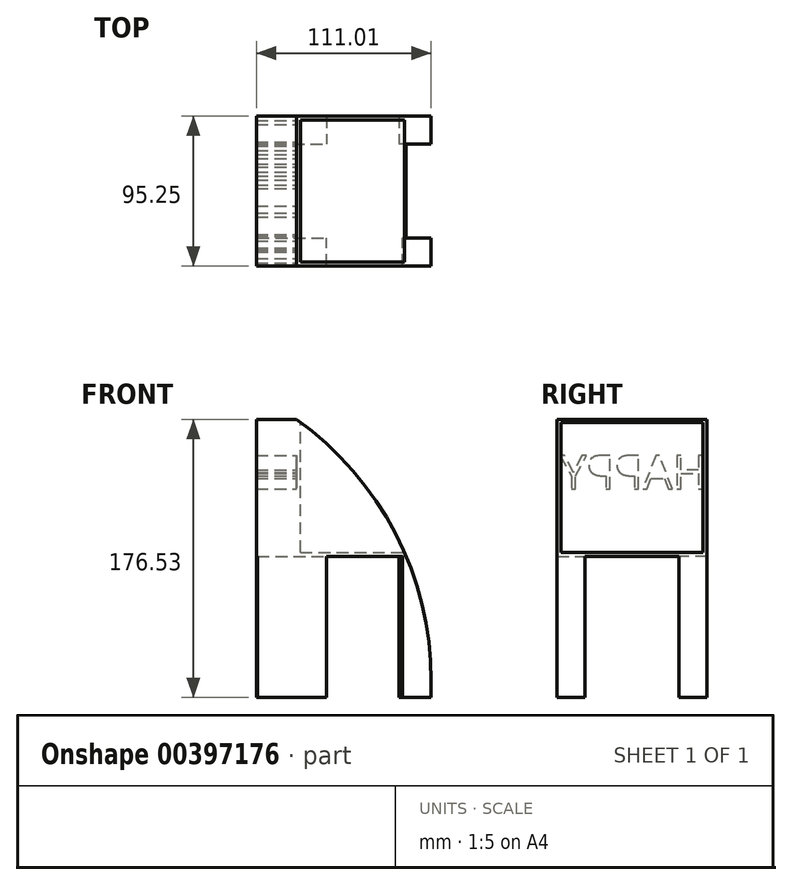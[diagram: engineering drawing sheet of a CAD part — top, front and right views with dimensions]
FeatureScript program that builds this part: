
annotation { "Feature Type Name" : "Feature", "Feature Type Description" : "" }
export const myFeature = defineFeature(function(context is Context, id is Id, definition is map)
    precondition{}
    {
        {
            var Q0;
            Q0=qCreatedBy(makeId("Front.planeOp"),FACE);
            var sketch = newSketch(context, id + "F0", { "sketchPlane" : qUnion([Q0])});
            skLineSegment(sketch, "E0.bottom", {"start": v(0, 0) * mm, "end": v(51.32, 0) * mm});
            skLineSegment(sketch, "E0.top", {"start": v(0, 35.31) * mm, "end": v(51.32, 35.31) * mm});
            skLineSegment(sketch, "E0.left", {"start": v(0, 0) * mm, "end": v(0, 35.31) * mm});
            skLineSegment(sketch, "E0.right", {"start": v(51.32, 0) * mm, "end": v(51.32, 35.31) * mm});
            skSolve(sketch);
        }
        {
            var Q0;
            Q0 = qSketchRegion(id + "F0", true);
            extrude(context, id + "F1", {"entities" : qUnion([Q0]), "depth" : 95.25 * mm});
        }
        {
            var Q0;
            Q0=makeQuery(id+"F1.opExtrude","SWEPT_FACE",FACE,{"disambiguationData":[OSD([sQuery(id+"F0.wireOp",EDGE,"E0.top")])]});
            extrude(context, id + "F2", {"entities" : qUnion([Q0]), "operationType" : NewBodyOperationType.ADD, "depth" : 51.56 * mm});
        }
        {
            var Q0;
            {var subQ0=sQuery(id+"F0.wireOp",EDGE,"E0.right");Q0=makeQuery(id+"F2.boolean.opBoolean","MERGE",FACE,{"derivedFrom":[makeQuery(id+"F1.opExtrude","SWEPT_FACE",FACE,{"disambiguationData":[OSD([subQ0])]}),makeQuery(id+"F2.opExtrude","SWEPT_FACE",FACE,{"disambiguationData":[OSD([sQuery(id+"F0.wireOp",EDGE,"E0.top"),subQ0])]})]});}
            extrude(context, id + "F3", {"entities" : qUnion([Q0]), "operationType" : NewBodyOperationType.ADD, "depth" : 34.3 * mm});
        }
        {
            var Q0;
            {var subQ0=sQuery(id+"F0.wireOp",EDGE,"E0.right");var subQ1=sQuery(id+"F0.wireOp",EDGE,"E0.top");Q0=makeQuery(id+"F3.boolean.opBoolean","MERGE",FACE,{"derivedFrom":[makeQuery(id+"F2.opExtrude","CAP_FACE",FACE,{"disambiguationData":[OSD([subQ1])],"isStart":false}),makeQuery(id+"F3.opExtrude","SWEPT_FACE",FACE,{"disambiguationData":[OSD([subQ1,subQ0]),TDD([makeQuery(id+"F2.opExtrude","CAP_EDGE",EDGE,{"disambiguationData":[OSD([subQ1,subQ0])],"isStart":false})])]})]});}
            shell(context, id + "F4", {"entities" : qUnion([Q0]), "thickness" : 2.54 * mm});
        }
        {
            var Q0;
            {var subQ0=sQuery(id+"F0.wireOp",EDGE,"E0.bottom");Q0=makeQuery(id+"F3.boolean.opBoolean","MERGE",FACE,{"derivedFrom":[makeQuery(id+"F1.opExtrude","SWEPT_FACE",FACE,{"disambiguationData":[OSD([subQ0])]}),makeQuery(id+"F3.opExtrude","SWEPT_FACE",FACE,{"disambiguationData":[OSD([subQ0,sQuery(id+"F0.wireOp",EDGE,"E0.right")])]})]});}
            var sketch = newSketch(context, id + "F5", { "sketchPlane" : qUnion([Q0])});
            skLineSegment(sketch, "E1.bottom", {"start": v(85.61, 95.25) * mm, "end": v(67.48, 95.25) * mm});
            skLineSegment(sketch, "E1.top", {"start": v(85.61, 77.42) * mm, "end": v(67.48, 77.42) * mm});
            skLineSegment(sketch, "E1.left", {"start": v(85.61, 95.25) * mm, "end": v(85.61, 77.42) * mm});
            skLineSegment(sketch, "E1.right", {"start": v(67.48, 95.25) * mm, "end": v(67.48, 77.42) * mm});
            skLineSegment(sketch, "E2.bottom", {"start": v(0.68, 95.25) * mm, "end": v(19.1, 95.25) * mm});
            skLineSegment(sketch, "E2.top", {"start": v(0.68, 77.42) * mm, "end": v(19.1, 77.42) * mm});
            skLineSegment(sketch, "E2.left", {"start": v(0.68, 95.25) * mm, "end": v(0.68, 77.42) * mm});
            skLineSegment(sketch, "E2.right", {"start": v(19.1, 95.25) * mm, "end": v(19.1, 77.42) * mm});
            skLineSegment(sketch, "E3.bottom", {"start": v(0, 0) * mm, "end": v(19.1, 0) * mm});
            skLineSegment(sketch, "E3.top", {"start": v(0, 17.72) * mm, "end": v(19.1, 17.72) * mm});
            skLineSegment(sketch, "E3.left", {"start": v(0, 0) * mm, "end": v(0, 17.72) * mm});
            skLineSegment(sketch, "E3.right", {"start": v(19.1, 0) * mm, "end": v(19.1, 17.72) * mm});
            skLineSegment(sketch, "E4.bottom", {"start": v(85.61, 0) * mm, "end": v(65.32, 0) * mm});
            skLineSegment(sketch, "E4.top", {"start": v(85.61, 17.72) * mm, "end": v(65.32, 17.72) * mm});
            skLineSegment(sketch, "E4.left", {"start": v(85.61, 0) * mm, "end": v(85.61, 17.72) * mm});
            skLineSegment(sketch, "E4.right", {"start": v(65.32, 0) * mm, "end": v(65.32, 17.72) * mm});
            skSolve(sketch);
        }
        {
            var Q0;
            Q0 = qSketchRegion(id + "F5", true);
            extrude(context, id + "F6", {"entities" : qUnion([Q0]), "operationType" : NewBodyOperationType.ADD, "depth" : 89.66 * mm});
        }
        {
            var Q0;
            {var subQ0=sQuery(id+"F0.wireOp",EDGE,"E0.right");var subQ1=sQuery(id+"F0.wireOp",EDGE,"E0.top");Q0=makeQuery(id+"F3.opExtrude","CAP_EDGE",EDGE,{"disambiguationData":[OSD([subQ1,subQ0]),TDD([makeQuery(id+"F2.opExtrude","CAP_EDGE",EDGE,{"disambiguationData":[OSD([subQ1,subQ0])],"isStart":false})])],"isStart":false});}
            fillet(context, id + "F7", {"entities" : qUnion([Q0]), "radius" : 203.2 * mm, "tangentPropagation" : true, "allowEdgeOverflow" : false});
        }
        {
            var Q0;
            {var subQ0=sQuery(id+"F0.wireOp",EDGE,"E0.left");Q0=makeQuery(id+"F6.boolean.opBoolean","MERGE",FACE,{"derivedFrom":[makeQuery(id+"F2.boolean.opBoolean","MERGE",FACE,{"derivedFrom":[makeQuery(id+"F1.opExtrude","SWEPT_FACE",FACE,{"disambiguationData":[OSD([subQ0])]}),makeQuery(id+"F2.opExtrude","SWEPT_FACE",FACE,{"disambiguationData":[OSD([sQuery(id+"F0.wireOp",EDGE,"E0.top"),subQ0])]})]}),makeQuery(id+"F6.opExtrude","SWEPT_FACE",FACE,{"disambiguationData":[OSD([sQuery(id+"F5.wireOp",EDGE,"E3.left")])]})]});}
            var sketch = newSketch(context, id + "F8", { "sketchPlane" : qUnion([Q0])});
            skText(sketch, "E5", { "text": "HAPPY\n", "fontName": "OpenSans-Regular.ttf"});
            const initialGuessF8  = {"E5": [0, 0.04276, 1, 0, 0.02143]};
            skSetInitialGuess(sketch, initialGuessF8);
            skSolve(sketch);
        }
        {
            var Q0;
            Q0=makeQuery(id+"F8.imprint","IMPRINT",FACE,{"disambiguationData":[TD([[makeQuery(id+"F8.imprint","IMPRINT",EDGE,{"derivedFrom":sQuery(id+"F8.wireOp",EDGE,"E5.sketch_text.stroke-0")}),1.0]])]});
            extrude(context, id + "F9", {"entities" : qUnion([Q0]), "operationType" : NewBodyOperationType.ADD, "depth" : 25.4 * mm});
        }
        {
            var Q0;
            Q0=makeQuery(id+"F6.opExtrude","SWEPT_FACE",FACE,{"disambiguationData":[OSD([sQuery(id+"F5.wireOp",EDGE,"E2.left")])]});
            var sketch = newSketch(context, id + "F10", { "sketchPlane" : qUnion([Q0])});
            skLineSegment(sketch, "E6.bottom", {"start": v(137.8, 28.12) * mm, "end": v(95.25, 28.12) * mm});
            skLineSegment(sketch, "E6.top", {"start": v(137.8, -89.66) * mm, "end": v(95.25, -89.66) * mm});
            skLineSegment(sketch, "E6.left", {"start": v(137.8, 28.12) * mm, "end": v(137.8, -89.66) * mm});
            skLineSegment(sketch, "E6.right", {"start": v(95.25, 28.12) * mm, "end": v(95.25, -89.66) * mm});
            skSolve(sketch);
        }
        {
            var Q0;
            {var subQ1=sQuery(id+"F5.wireOp",EDGE,"E2.left");var subQ2=makeQuery(id+"F6.opExtrude","CAP_EDGE",EDGE,{"disambiguationData":[OSD([subQ1])],"isStart":false});Q0=makeQuery(id+"F10.imprint","IMPRINT",FACE,{"disambiguationData":[TD([[makeQuery(id+"F10.imprint","IMPRINT",EDGE,{"derivedFrom":subQ2}),-1.0]])]});}
            extrude(context, id + "F11", {"entities" : qUnion([Q0]), "operationType" : NewBodyOperationType.ADD, "depth" : 25.4 * mm});
        }
    });
